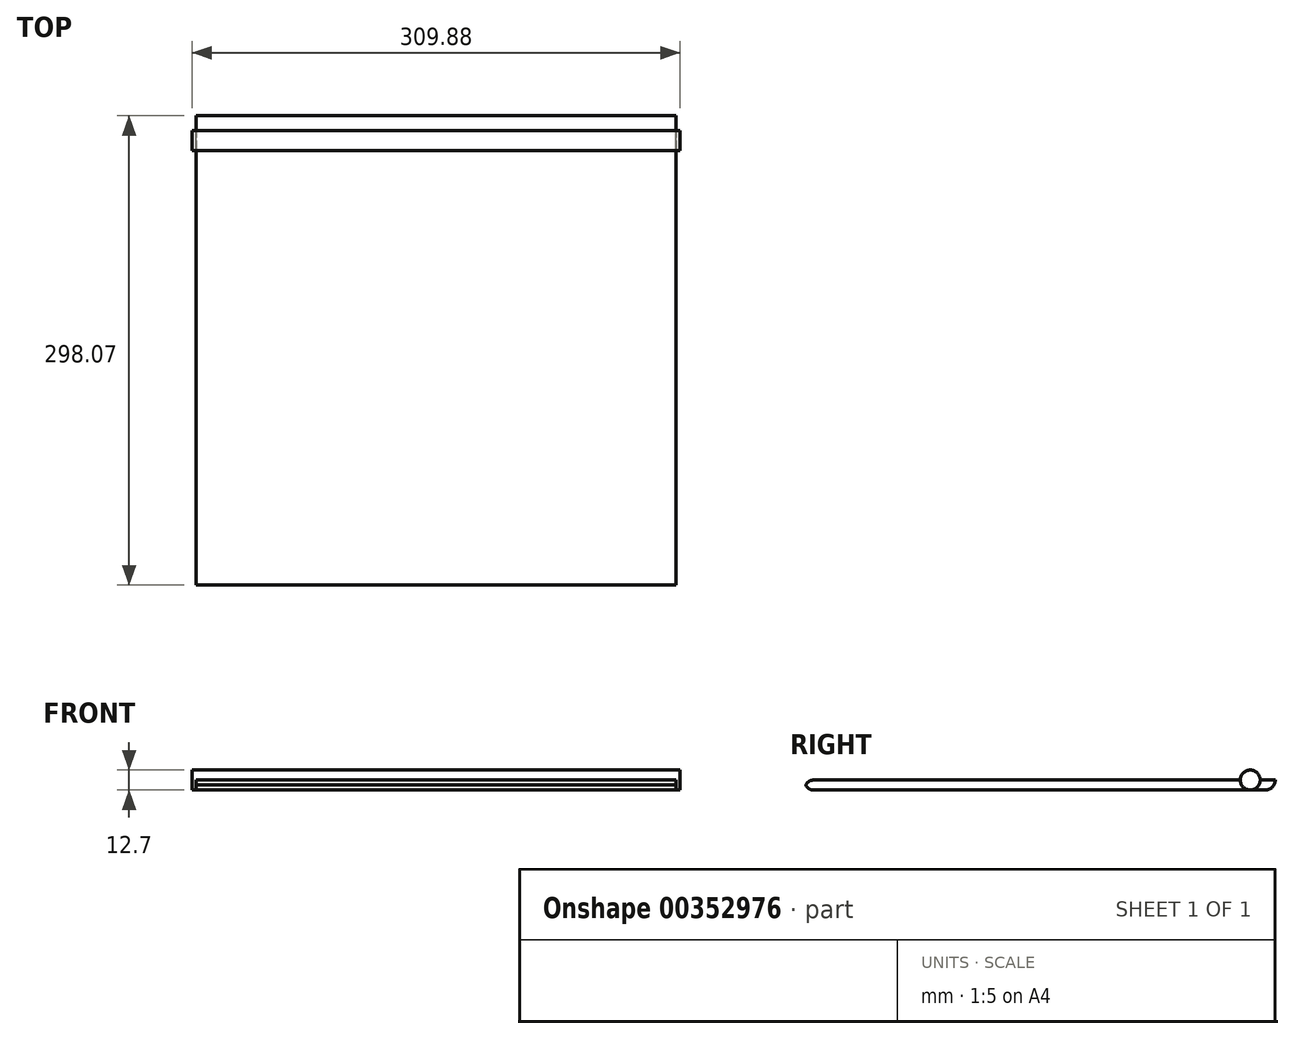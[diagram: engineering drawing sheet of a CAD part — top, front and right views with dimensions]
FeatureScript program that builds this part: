
annotation { "Feature Type Name" : "Feature", "Feature Type Description" : "" }
export const myFeature = defineFeature(function(context is Context, id is Id, definition is map)
    precondition{}
    {
        {
            var Q0;
            Q0=qCreatedBy(makeId("Top.planeOp"),FACE);
            var sketch = newSketch(context, id + "F0", { "sketchPlane" : qUnion([Q0])});
            skLineSegment(sketch, "E0.bottom", {"start": v(152.4, 149.23) * mm, "end": v(-152.4, 149.23) * mm});
            skLineSegment(sketch, "E0.top", {"start": v(152.4, -149.23) * mm, "end": v(-152.4, -149.23) * mm});
            skLineSegment(sketch, "E0.left", {"start": v(152.4, 149.23) * mm, "end": v(152.4, -149.23) * mm});
            skLineSegment(sketch, "E0.right", {"start": v(-152.4, 149.23) * mm, "end": v(-152.4, -149.23) * mm});
            skPoint(sketch, "E0.middle", {"position": v(0, 0) * mm});
            skSolve(sketch);
        }
        {
            var Q0;
            Q0 = qSketchRegion(id + "F0", true);
            extrude(context, id + "F1", {"entities" : qUnion([Q0]), "depth" : 6.35 * mm});
        }
        {
            var Q0;
            Q0=makeQuery(id+"F1.opExtrude","CAP_EDGE",EDGE,{"disambiguationData":[OSD([sQuery(id+"F0.wireOp",EDGE,"E0.bottom")])],"isStart":true});
            fillet(context, id + "F2", {"entities" : qUnion([Q0]), "radius" : 6.35 * mm, "tangentPropagation" : true, "allowEdgeOverflow" : false});
        }
        {
            var Q0;
            Q0=makeQuery(id+"F1.opExtrude","SWEPT_FACE",FACE,{"disambiguationData":[OSD([sQuery(id+"F0.wireOp",EDGE,"E0.left")])]});
            var sketch = newSketch(context, id + "F3", { "sketchPlane" : qUnion([Q0])});
            skCircle(sketch, "E1", {"center": v(133.35, 6.35) * mm, "radius": 6.35 * mm});
            skSolve(sketch);
        }
        {
            var Q0;
            Q0 = qSketchRegion(id + "F3", true);
            extrude(context, id + "F4", {"entities" : qUnion([Q0]), "operationType" : NewBodyOperationType.ADD, "depth" : 2.54 * mm, "hasSecondDirection" : true, "secondDirectionOppositeDirection" : true, "secondDirectionDepth" : 307.34 * mm});
        }
        {
            var Q0;
            Q0=makeQuery(id+"F1.opExtrude","CAP_EDGE",EDGE,{"disambiguationData":[OSD([sQuery(id+"F0.wireOp",EDGE,"E0.top")])],"isStart":true});
            var Q1;
            Q1=makeQuery(id+"F1.opExtrude","CAP_EDGE",EDGE,{"disambiguationData":[OSD([sQuery(id+"F0.wireOp",EDGE,"E0.top")])],"isStart":false});
            fillet(context, id + "F5", {"entities" : qUnion([Q0, Q1]), "radius" : 5.08 * mm, "tangentPropagation" : true, "allowEdgeOverflow" : false});
        }
    });
